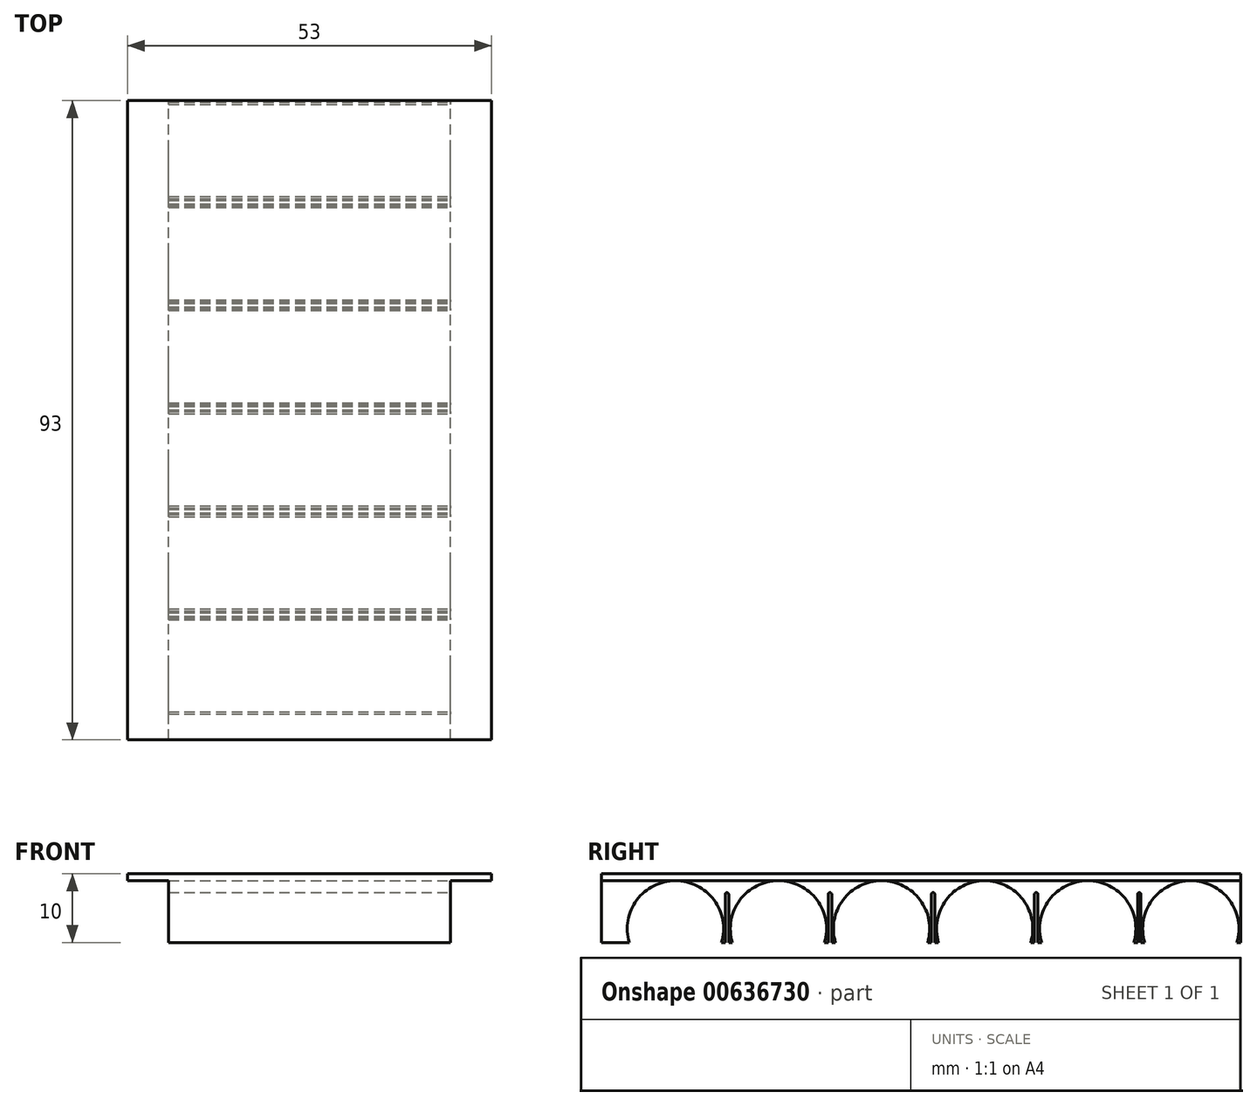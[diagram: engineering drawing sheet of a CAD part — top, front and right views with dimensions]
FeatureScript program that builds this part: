
annotation { "Feature Type Name" : "Feature", "Feature Type Description" : "" }
export const myFeature = defineFeature(function(context is Context, id is Id, definition is map)
    precondition{}
    {
        {
            var Q0;
            Q0=qCreatedBy(makeId("Top.planeOp"),FACE);
            var sketch = newSketch(context, id + "F0", { "sketchPlane" : qUnion([Q0])});
            skLineSegment(sketch, "E0.bottom", {"start": v(0, 0) * mm, "end": v(-53, 0) * mm});
            skLineSegment(sketch, "E0.top", {"start": v(0, 93) * mm, "end": v(-53, 93) * mm});
            skLineSegment(sketch, "E0.left", {"start": v(0, 0) * mm, "end": v(0, 93) * mm});
            skLineSegment(sketch, "E0.right", {"start": v(-53, 0) * mm, "end": v(-53, 93) * mm});
            skSolve(sketch);
        }
        {
            var Q0;
            Q0 = qSketchRegion(id + "F0", true);
            extrude(context, id + "F1", {"entities" : qUnion([Q0]), "depth" : 1 * mm, "offsetDistance" : 25 * mm});
        }
        {
            var Q0;
            Q0=makeQuery(id+"F1.opExtrude","CAP_FACE",FACE,{"disambiguationData":[OSD([sQuery(id+"F0.wireOp",EDGE,"E0.bottom"),sQuery(id+"F0.wireOp",EDGE,"E0.top"),sQuery(id+"F0.wireOp",EDGE,"E0.left"),sQuery(id+"F0.wireOp",EDGE,"E0.right")])],"isStart":false});
            var sketch = newSketch(context, id + "F2", { "sketchPlane" : qUnion([Q0])});
            skLineSegment(sketch, "E1", {"start": v(-26.5, 93) * mm, "end": v(-26.5, 46.5) * mm, "construction": true});
            skLineSegment(sketch, "E2", {"start": v(0, 46.5) * mm, "end": v(-26.5, 46.5) * mm, "construction": true});
            skSolve(sketch);
        }
        {
            var Q0;
            Q0=makeQuery(id+"F2.imprint","IMPRINT",FACE,{"disambiguationData":[TD([[makeQuery(id+"F2.imprint","IMPRINT",EDGE,{"derivedFrom":makeQuery(id+"F1.opExtrude","CAP_EDGE",EDGE,{"disambiguationData":[OSD([sQuery(id+"F0.wireOp",EDGE,"E0.bottom")])],"isStart":false})}),-1.0]])]});
            extrude(context, id + "F3", {"entities" : qUnion([Q0]), "operationType" : NewBodyOperationType.ADD, "oppositeDirection" : true, "depth" : 10 * mm, "offsetDistance" : 25 * mm});
        }
        {
            var Q0;
            {var subQ0=sQuery(id+"F0.wireOp",EDGE,"E0.left");Q0=makeQuery(id+"F3.boolean.opBoolean","MERGE",FACE,{"derivedFrom":[makeQuery(id+"F1.opExtrude","SWEPT_FACE",FACE,{"disambiguationData":[OSD([subQ0])]}),makeQuery(id+"F3.opExtrude","SWEPT_FACE",FACE,{"disambiguationData":[OSD([subQ0])]})]});}
            var sketch = newSketch(context, id + "F4", { "sketchPlane" : qUnion([Q0])});
            skLineSegment(sketch, "E3.bottom", {"start": v(0, 0) * mm, "end": v(93, 0) * mm, "construction": true});
            skLineSegment(sketch, "E3.top", {"start": v(0, -9) * mm, "end": v(93, -9) * mm, "construction": true});
            skLineSegment(sketch, "E3.left", {"start": v(0, 0) * mm, "end": v(0, -9) * mm, "construction": true});
            skLineSegment(sketch, "E3.right", {"start": v(93, 0) * mm, "end": v(93, -9) * mm, "construction": true});
            skLineSegment(sketch, "E4", {"start": v(46.5, 0) * mm, "end": v(46.5, -9) * mm, "construction": true});
            skLineSegment(sketch, "E5", {"start": v(46.5, -4.5) * mm, "end": v(0, -4.5) * mm, "construction": true});
            skArc(sketch, "E6", {"start": v(92.46, -9) * mm, "mid": v(85.75, 0) * mm, "end": v(79.04, -9) * mm});
            skArc(sketch, "E7", {"start": v(77.46, -9) * mm, "mid": v(70.75, 0) * mm, "end": v(64.04, -9) * mm});
            skLineSegment(sketch, "E8", {"start": v(63.75, -7) * mm, "end": v(62.75, -7) * mm});
            skArc(sketch, "E9", {"start": v(62.46, -9) * mm, "mid": v(55.75, 0) * mm, "end": v(49.04, -9) * mm});
            skArc(sketch, "E10", {"start": v(47.46, -9) * mm, "mid": v(40.75, 0) * mm, "end": v(34.04, -9) * mm});
            skArc(sketch, "E11", {"start": v(32.46, -9) * mm, "mid": v(25.75, 0) * mm, "end": v(19.04, -9) * mm});
            skArc(sketch, "E12", {"start": v(17.46, -9) * mm, "mid": v(10.75, 0) * mm, "end": v(4.04, -9) * mm});
            skLineSegment(sketch, "E13", {"start": v(92.75, -7) * mm, "end": v(93, -7) * mm});
            skLineSegment(sketch, "E14", {"start": v(92.75, -7) * mm, "end": v(98.08, -7) * mm});
            skLineSegment(sketch, "E15", {"start": v(98.08, -7) * mm, "end": v(98.08, -22.46) * mm});
            skLineSegment(sketch, "E16", {"start": v(98.08, -22.46) * mm, "end": v(-7.47, -22.46) * mm});
            skLineSegment(sketch, "E17", {"start": v(-7.47, -22.46) * mm, "end": v(-7.47, -7.75) * mm});
            skLineSegment(sketch, "E18", {"start": v(-7.47, -7.75) * mm, "end": v(3.79, -7.75) * mm});
            skLineSegment(sketch, "E19", {"start": v(0, 0) * mm, "end": v(0, -7) * mm, "construction": true});
            skLineSegment(sketch, "E20", {"start": v(0, -7) * mm, "end": v(92.75, -7) * mm, "construction": true});
            skLineSegment(sketch, "E21", {"start": v(17.75, -7) * mm, "end": v(18, -7) * mm, "construction": true});
            skLineSegment(sketch, "E22", {"start": v(18, -7) * mm, "end": v(18.5, -7) * mm, "construction": true});
            skLineSegment(sketch, "E23", {"start": v(18.5, -7) * mm, "end": v(18.5, -2) * mm});
            skLineSegment(sketch, "E24", {"start": v(18, -2) * mm, "end": v(18, -9) * mm});
            skLineSegment(sketch, "E25", {"start": v(18, -9) * mm, "end": v(18.5, -9) * mm});
            skLineSegment(sketch, "E26", {"start": v(18.5, -9) * mm, "end": v(18.5, -7) * mm});
            skLineSegment(sketch, "E27.1.0.0", {"start": v(33, -2) * mm, "end": v(33, -9) * mm});
            skLineSegment(sketch, "E27.1.0.1", {"start": v(33.5, -7) * mm, "end": v(33.5, -2) * mm});
            skLineSegment(sketch, "E27.1.0.2", {"start": v(33.5, -9) * mm, "end": v(33.5, -7) * mm});
            skLineSegment(sketch, "E27.2.0.0", {"start": v(48, -2) * mm, "end": v(48, -9) * mm});
            skLineSegment(sketch, "E27.2.0.1", {"start": v(48.5, -7) * mm, "end": v(48.5, -2) * mm});
            skLineSegment(sketch, "E27.2.0.2", {"start": v(48.5, -9) * mm, "end": v(48.5, -7) * mm});
            skLineSegment(sketch, "E27.3.0.0", {"start": v(63, -2) * mm, "end": v(63, -9) * mm});
            skLineSegment(sketch, "E27.3.0.1", {"start": v(63.5, -7) * mm, "end": v(63.5, -2) * mm});
            skLineSegment(sketch, "E27.3.0.2", {"start": v(63.5, -9) * mm, "end": v(63.5, -7) * mm});
            skLineSegment(sketch, "E27.4.0.0", {"start": v(78, -2) * mm, "end": v(78, -9) * mm});
            skLineSegment(sketch, "E27.4.0.1", {"start": v(78.5, -7) * mm, "end": v(78.5, -2) * mm});
            skLineSegment(sketch, "E27.4.0.2", {"start": v(78.5, -9) * mm, "end": v(78.5, -7) * mm});
            skLineSegment(sketch, "E27.direction1", {"start": v(18, -9) * mm, "end": v(33, -9) * mm, "construction": true});
            skArc(sketch, "E28", {"start": v(18.5, -2) * mm, "mid": v(18.25, -1.75) * mm, "end": v(18, -2) * mm});
            skArc(sketch, "E29.1.0.0", {"start": v(33.5, -2) * mm, "mid": v(33.25, -1.75) * mm, "end": v(33, -2) * mm});
            skArc(sketch, "E29.2.0.0", {"start": v(48.5, -2) * mm, "mid": v(48.25, -1.75) * mm, "end": v(48, -2) * mm});
            skArc(sketch, "E29.3.0.0", {"start": v(63.5, -2) * mm, "mid": v(63.25, -1.75) * mm, "end": v(63, -2) * mm});
            skArc(sketch, "E29.4.0.0", {"start": v(78.5, -2) * mm, "mid": v(78.25, -1.75) * mm, "end": v(78, -2) * mm});
            skLineSegment(sketch, "E29.direction1", {"start": v(18, -2) * mm, "end": v(33, -2) * mm, "construction": true});
            skSolve(sketch);
        }
        {
            var Q0;
            {var subQ19=sQuery(id+"F4.wireOp",EDGE,"E15");Q0=makeQuery(id+"F4.imprint","IMPRINT",FACE,{"disambiguationData":[TD([[makeQuery(id+"F4.imprint","IMPRINT",EDGE,{"derivedFrom":subQ19}),-1.0]])]});}
            var Q1;
            {var subQ0=sQuery(id+"F4.wireOp",EDGE,"E6");var subQ1=makeQuery(id+"F3.opExtrude","CAP_EDGE",EDGE,{"disambiguationData":[OSD([sQuery(id+"F0.wireOp",EDGE,"E0.left")])],"isStart":false});var subQ2=makeQuery(id+"F4.imprint","INTERSECT",VERTEX,{"disambiguationData":[OD(0.0)],"derivedFrom":[subQ1,subQ0]});Q1=makeQuery(id+"F4.imprint","IMPRINT",FACE,{"disambiguationData":[TD([[makeQuery(id+"F4.imprint","IMPRINT",EDGE,{"disambiguationData":[TD([[subQ2,-1.0]])],"derivedFrom":subQ0}),1.0]])]});}
            var Q2;
            {var subQ0=sQuery(id+"F4.wireOp",EDGE,"E7");var subQ1=makeQuery(id+"F3.opExtrude","CAP_EDGE",EDGE,{"disambiguationData":[OSD([sQuery(id+"F0.wireOp",EDGE,"E0.left")])],"isStart":false});var subQ2=makeQuery(id+"F4.imprint","INTERSECT",VERTEX,{"disambiguationData":[OD(0.0)],"derivedFrom":[subQ1,subQ0]});Q2=makeQuery(id+"F4.imprint","IMPRINT",FACE,{"disambiguationData":[TD([[makeQuery(id+"F4.imprint","IMPRINT",EDGE,{"disambiguationData":[TD([[subQ2,-1.0]])],"derivedFrom":subQ0}),1.0]])]});}
            var Q3;
            {var subQ0=sQuery(id+"F4.wireOp",EDGE,"E10");Q3=makeQuery(id+"F4.imprint","IMPRINT",FACE,{"disambiguationData":[TD([[makeQuery(id+"F4.imprint","IMPRINT",EDGE,{"derivedFrom":subQ0}),1.0]])]});}
            var Q4;
            {var subQ0=sQuery(id+"F4.wireOp",EDGE,"E9");var subQ1=makeQuery(id+"F4.imprint","INTERSECT",VERTEX,{"derivedFrom":[sQuery(id+"F4.wireOp",EDGE,"E8"),subQ0]});Q4=makeQuery(id+"F4.imprint","IMPRINT",FACE,{"disambiguationData":[TD([[makeQuery(id+"F4.imprint","IMPRINT",EDGE,{"disambiguationData":[TD([[subQ1,1.0]])],"derivedFrom":subQ0}),1.0]])]});}
            var Q5;
            {var subQ0=sQuery(id+"F4.wireOp",EDGE,"E11");Q5=makeQuery(id+"F4.imprint","IMPRINT",FACE,{"disambiguationData":[TD([[makeQuery(id+"F4.imprint","IMPRINT",EDGE,{"derivedFrom":subQ0}),1.0]])]});}
            var Q6;
            {var subQ0=sQuery(id+"F4.wireOp",EDGE,"E12");var subQ1=makeQuery(id+"F3.opExtrude","CAP_EDGE",EDGE,{"disambiguationData":[OSD([sQuery(id+"F0.wireOp",EDGE,"E0.left")])],"isStart":false});var subQ2=makeQuery(id+"F4.imprint","INTERSECT",VERTEX,{"disambiguationData":[OD(0.0)],"derivedFrom":[subQ1,subQ0]});Q6=makeQuery(id+"F4.imprint","IMPRINT",FACE,{"disambiguationData":[TD([[makeQuery(id+"F4.imprint","IMPRINT",EDGE,{"disambiguationData":[TD([[subQ2,-1.0]])],"derivedFrom":subQ0}),1.0]])]});}
            extrude(context, id + "F5", {"entities" : qUnion([Q0, Q1, Q2, Q3, Q4, Q5, Q6]), "operationType" : NewBodyOperationType.REMOVE, "oppositeDirection" : true, "depth" : 70 * mm, "offsetDistance" : 25 * mm});
        }
        {
            var Q0;
            {var subQ0=sQuery(id+"F0.wireOp",EDGE,"E0.bottom");var subQ1=sQuery(id+"F0.wireOp",EDGE,"E0.left");var subQ2=sQuery(id+"F0.wireOp",EDGE,"E0.right");Q0=makeQuery(id+"F5.boolean.opBoolean","SPLIT",FACE,{"disambiguationData":[TD([makeQuery(id+"F1.opExtrude","SWEPT_FACE",FACE,{"disambiguationData":[OSD([subQ0])]}),makeQuery(id+"F1.opExtrude","SWEPT_FACE",FACE,{"disambiguationData":[OSD([subQ1])]}),makeQuery(id+"F1.opExtrude","SWEPT_FACE",FACE,{"disambiguationData":[OSD([subQ2])]}),makeQuery(id+"F3.opExtrude","SWEPT_FACE",FACE,{"disambiguationData":[OSD([subQ0])]}),makeQuery(id+"F3.opExtrude","SWEPT_FACE",FACE,{"disambiguationData":[OSD([subQ1])]}),makeQuery(id+"F3.opExtrude","SWEPT_FACE",FACE,{"disambiguationData":[OSD([subQ2])]}),makeQuery(id+"F5.opExtrude","SWEPT_FACE",FACE,{"disambiguationData":[OSD([sQuery(id+"F4.wireOp",EDGE,"E12")])]})])],"derivedFrom":makeQuery(id+"F3.opExtrude","CAP_FACE",FACE,{"disambiguationData":[OSD([subQ0,sQuery(id+"F0.wireOp",EDGE,"E0.top"),subQ1,subQ2])],"isStart":false})});}
            var sketch = newSketch(context, id + "F6", { "sketchPlane" : qUnion([Q0])});
            skLineSegment(sketch, "E30.bottom", {"start": v(0, 0) * mm, "end": v(-6, 0) * mm});
            skLineSegment(sketch, "E30.top", {"start": v(0, -100) * mm, "end": v(-6, -100) * mm});
            skLineSegment(sketch, "E30.left", {"start": v(0, 0) * mm, "end": v(0, -100) * mm});
            skLineSegment(sketch, "E30.right", {"start": v(-6, 0) * mm, "end": v(-6, -100) * mm});
            skLineSegment(sketch, "E31.bottom", {"start": v(-53, 0) * mm, "end": v(-47, 0) * mm});
            skLineSegment(sketch, "E31.top", {"start": v(-53, -100) * mm, "end": v(-47, -100) * mm});
            skLineSegment(sketch, "E31.left", {"start": v(-53, 0) * mm, "end": v(-53, -100) * mm});
            skLineSegment(sketch, "E31.right", {"start": v(-47, 0) * mm, "end": v(-47, -100) * mm});
            skSolve(sketch);
        }
        {
            var Q0;
            {var subQ0=sQuery(id+"F6.wireOp",EDGE,"E31.top");Q0=makeQuery(id+"F6.imprint","IMPRINT",FACE,{"disambiguationData":[TD([[makeQuery(id+"F6.imprint","IMPRINT",EDGE,{"derivedFrom":subQ0}),1.0]])]});}
            var Q1;
            {var subQ0=sQuery(id+"F6.wireOp",EDGE,"E31.bottom");Q1=makeQuery(id+"F6.imprint","IMPRINT",FACE,{"disambiguationData":[TD([[makeQuery(id+"F6.imprint","IMPRINT",EDGE,{"derivedFrom":subQ0}),1.0]])]});}
            var Q2;
            {var subQ0=sQuery(id+"F6.wireOp",EDGE,"E30.bottom");Q2=makeQuery(id+"F6.imprint","IMPRINT",FACE,{"disambiguationData":[TD([[makeQuery(id+"F6.imprint","IMPRINT",EDGE,{"derivedFrom":subQ0}),1.0]])]});}
            var Q3;
            {var subQ0=sQuery(id+"F6.wireOp",EDGE,"E30.top");Q3=makeQuery(id+"F6.imprint","IMPRINT",FACE,{"disambiguationData":[TD([[makeQuery(id+"F6.imprint","IMPRINT",EDGE,{"derivedFrom":subQ0}),-1.0]])]});}
            extrude(context, id + "F7", {"entities" : qUnion([Q0, Q1, Q2, Q3]), "operationType" : NewBodyOperationType.REMOVE, "oppositeDirection" : true, "depth" : 9 * mm, "offsetDistance" : 25 * mm});
        }
        {
            var Q0;
            Q0=makeQuery(id+"F4.imprint","IMPRINT",FACE,{"disambiguationData":[TD([[makeQuery(id+"F4.imprint","IMPRINT",EDGE,{"derivedFrom":sQuery(id+"F4.wireOp",EDGE,"E23")}),1.0]])]});
            var Q1;
            {var subQ1=sQuery(id+"F4.wireOp",EDGE,"E27.1.0.0");Q1=makeQuery(id+"F4.imprint","IMPRINT",FACE,{"disambiguationData":[TD([[makeQuery(id+"F4.imprint","IMPRINT",EDGE,{"derivedFrom":subQ1}),1.0]])]});}
            var Q2;
            {var subQ1=sQuery(id+"F4.wireOp",EDGE,"E27.2.0.0");Q2=makeQuery(id+"F4.imprint","IMPRINT",FACE,{"disambiguationData":[TD([[makeQuery(id+"F4.imprint","IMPRINT",EDGE,{"derivedFrom":subQ1}),1.0]])]});}
            var Q3;
            {var subQ1=sQuery(id+"F4.wireOp",EDGE,"E27.3.0.1");Q3=makeQuery(id+"F4.imprint","IMPRINT",FACE,{"disambiguationData":[TD([[makeQuery(id+"F4.imprint","IMPRINT",EDGE,{"derivedFrom":subQ1}),1.0]])]});}
            var Q4;
            {var subQ1=sQuery(id+"F4.wireOp",EDGE,"E27.4.0.0");Q4=makeQuery(id+"F4.imprint","IMPRINT",FACE,{"disambiguationData":[TD([[makeQuery(id+"F4.imprint","IMPRINT",EDGE,{"derivedFrom":subQ1}),1.0]])]});}
            var Q5;
            {var subQ0=sQuery(id+"F4.wireOp",EDGE,"E27.3.0.2");var subQ1=sQuery(id+"F4.wireOp",EDGE,"E8");var subQ2=makeQuery(id+"F4.imprint","INTERSECT",VERTEX,{"derivedFrom":[subQ1,subQ0]});Q5=makeQuery(id+"F4.imprint","IMPRINT",FACE,{"disambiguationData":[TD([[makeQuery(id+"F4.imprint","IMPRINT",EDGE,{"disambiguationData":[TD([[subQ2,-1.0]])],"derivedFrom":subQ1}),1.0]])]});}
            extrude(context, id + "F8", {"entities" : qUnion([Q0, Q1, Q2, Q3, Q4, Q5]), "operationType" : NewBodyOperationType.REMOVE, "oppositeDirection" : true, "depth" : 60 * mm, "offsetDistance" : 25 * mm});
        }
    });
